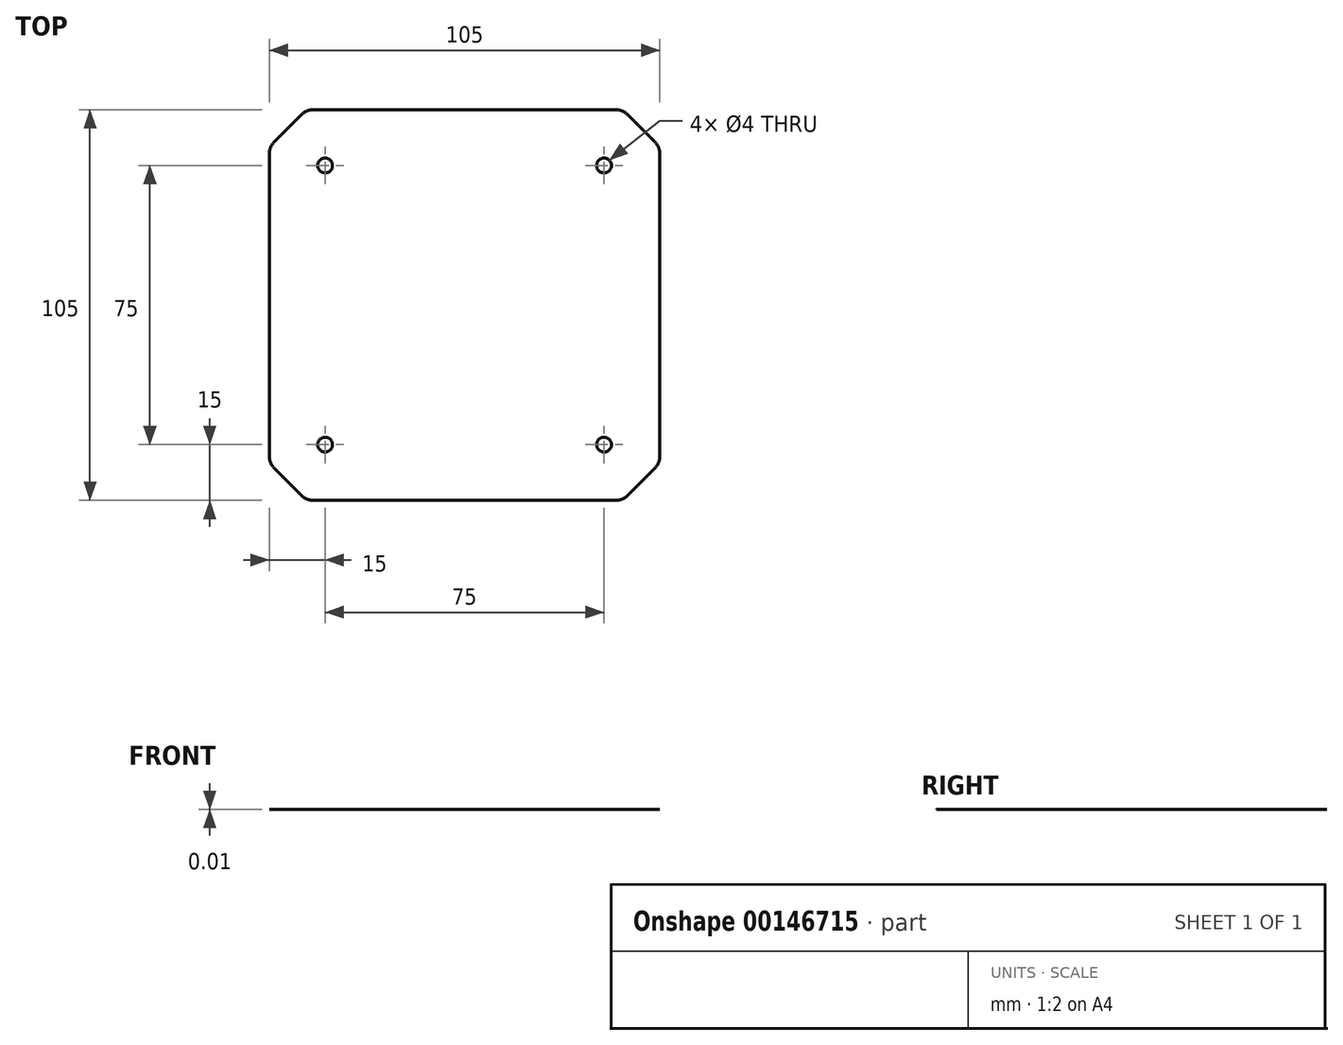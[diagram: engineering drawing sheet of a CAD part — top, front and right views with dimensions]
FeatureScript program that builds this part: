
annotation { "Feature Type Name" : "Feature", "Feature Type Description" : "" }
export const myFeature = defineFeature(function(context is Context, id is Id, definition is map)
    precondition{}
    {
        {
            var Q0;
            Q0=qCreatedBy(makeId("Top.planeOp"),FACE);
            var sketch = newSketch(context, id + "F0", { "sketchPlane" : qUnion([Q0])});
            skCircle(sketch, "E0", {"center": v(-37.5, 37.5) * mm, "radius": 2 * mm});
            skCircle(sketch, "E1.MirrorC", {"center": v(37.5, 37.5) * mm, "radius": 2 * mm});
            skCircle(sketch, "E2.MirrorC", {"center": v(-37.5, -37.5) * mm, "radius": 2 * mm});
            skCircle(sketch, "E3.MirrorC", {"center": v(37.5, -37.5) * mm, "radius": 2 * mm});
            skLineSegment(sketch, "E4.bottom", {"start": v(-52.5, 52.5) * mm, "end": v(52.5, 52.5) * mm});
            skLineSegment(sketch, "E4.top", {"start": v(-52.5, -52.5) * mm, "end": v(52.5, -52.5) * mm});
            skLineSegment(sketch, "E4.left", {"start": v(-52.5, 52.5) * mm, "end": v(-52.5, -52.5) * mm});
            skLineSegment(sketch, "E4.right", {"start": v(52.5, 52.5) * mm, "end": v(52.5, -52.5) * mm});
            skSolve(sketch);
        }
        {
            var Q0;
            Q0=makeQuery(id+"F0.imprint","IMPRINT",FACE,{"disambiguationData":[TD([[makeQuery(id+"F0.imprint","IMPRINT",EDGE,{"derivedFrom":sQuery(id+"F0.wireOp",EDGE,"E0")}),-1.0]])]});
            extrude(context, id + "F1", {"entities" : qUnion([Q0]), "depth" : 1 / 101.6 * mm});
        }
        {
            var Q0;
            Q0=makeQuery(id+"F1.opExtrude","SWEPT_EDGE",EDGE,{"disambiguationData":[OSD([sQuery(id+"F0.wireOp",EDGE,"E4.top"),sQuery(id+"F0.wireOp",EDGE,"E4.left")])]});
            var Q1;
            Q1=makeQuery(id+"F1.opExtrude","SWEPT_EDGE",EDGE,{"disambiguationData":[OSD([sQuery(id+"F0.wireOp",EDGE,"E4.top"),sQuery(id+"F0.wireOp",EDGE,"E4.right")])]});
            var Q2;
            Q2=makeQuery(id+"F1.opExtrude","SWEPT_EDGE",EDGE,{"disambiguationData":[OSD([sQuery(id+"F0.wireOp",EDGE,"E4.bottom"),sQuery(id+"F0.wireOp",EDGE,"E4.right")])]});
            var Q3;
            Q3=makeQuery(id+"F1.opExtrude","SWEPT_EDGE",EDGE,{"disambiguationData":[OSD([sQuery(id+"F0.wireOp",EDGE,"E4.bottom"),sQuery(id+"F0.wireOp",EDGE,"E4.left")])]});
            chamfer(context, id + "F2", {"entities" : qUnion([Q0, Q1, Q2, Q3]), "width" : 10 * mm, "tangentPropagation" : true});
        }
        {
            var Q0;
            {var subQ0=sQuery(id+"F0.wireOp",EDGE,"E4.right");Q0=makeQuery(id+"F2.opChamfer","BLEND_EDGE",EDGE,{"blendedFrom":[makeQuery(id+"F1.opExtrude","SWEPT_EDGE",EDGE,{"disambiguationData":[OSD([sQuery(id+"F0.wireOp",EDGE,"E4.bottom"),subQ0])]}),makeQuery(id+"F1.opExtrude","SWEPT_FACE",FACE,{"disambiguationData":[OSD([subQ0])]})],"blendedInto":[makeQuery(id+"F1.opExtrude","SWEPT_FACE",FACE,{"disambiguationData":[OSD([subQ0])]})]});}
            var Q1;
            {var subQ0=sQuery(id+"F0.wireOp",EDGE,"E4.bottom");Q1=makeQuery(id+"F2.opChamfer","BLEND_EDGE",EDGE,{"blendedFrom":[makeQuery(id+"F1.opExtrude","SWEPT_EDGE",EDGE,{"disambiguationData":[OSD([subQ0,sQuery(id+"F0.wireOp",EDGE,"E4.right")])]}),makeQuery(id+"F1.opExtrude","SWEPT_FACE",FACE,{"disambiguationData":[OSD([subQ0])]})],"blendedInto":[makeQuery(id+"F1.opExtrude","SWEPT_FACE",FACE,{"disambiguationData":[OSD([subQ0])]})]});}
            var Q2;
            {var subQ0=sQuery(id+"F0.wireOp",EDGE,"E4.bottom");Q2=makeQuery(id+"F2.opChamfer","BLEND_EDGE",EDGE,{"blendedFrom":[makeQuery(id+"F1.opExtrude","SWEPT_EDGE",EDGE,{"disambiguationData":[OSD([subQ0,sQuery(id+"F0.wireOp",EDGE,"E4.left")])]}),makeQuery(id+"F1.opExtrude","SWEPT_FACE",FACE,{"disambiguationData":[OSD([subQ0])]})],"blendedInto":[makeQuery(id+"F1.opExtrude","SWEPT_FACE",FACE,{"disambiguationData":[OSD([subQ0])]})]});}
            var Q3;
            {var subQ0=sQuery(id+"F0.wireOp",EDGE,"E4.left");Q3=makeQuery(id+"F2.opChamfer","BLEND_EDGE",EDGE,{"blendedFrom":[makeQuery(id+"F1.opExtrude","SWEPT_EDGE",EDGE,{"disambiguationData":[OSD([sQuery(id+"F0.wireOp",EDGE,"E4.bottom"),subQ0])]}),makeQuery(id+"F1.opExtrude","SWEPT_FACE",FACE,{"disambiguationData":[OSD([subQ0])]})],"blendedInto":[makeQuery(id+"F1.opExtrude","SWEPT_FACE",FACE,{"disambiguationData":[OSD([subQ0])]})]});}
            var Q4;
            {var subQ0=sQuery(id+"F0.wireOp",EDGE,"E4.left");Q4=makeQuery(id+"F2.opChamfer","BLEND_EDGE",EDGE,{"blendedFrom":[makeQuery(id+"F1.opExtrude","SWEPT_EDGE",EDGE,{"disambiguationData":[OSD([sQuery(id+"F0.wireOp",EDGE,"E4.top"),subQ0])]}),makeQuery(id+"F1.opExtrude","SWEPT_FACE",FACE,{"disambiguationData":[OSD([subQ0])]})],"blendedInto":[makeQuery(id+"F1.opExtrude","SWEPT_FACE",FACE,{"disambiguationData":[OSD([subQ0])]})]});}
            var Q5;
            {var subQ0=sQuery(id+"F0.wireOp",EDGE,"E4.top");Q5=makeQuery(id+"F2.opChamfer","BLEND_EDGE",EDGE,{"blendedFrom":[makeQuery(id+"F1.opExtrude","SWEPT_EDGE",EDGE,{"disambiguationData":[OSD([subQ0,sQuery(id+"F0.wireOp",EDGE,"E4.left")])]}),makeQuery(id+"F1.opExtrude","SWEPT_FACE",FACE,{"disambiguationData":[OSD([subQ0])]})],"blendedInto":[makeQuery(id+"F1.opExtrude","SWEPT_FACE",FACE,{"disambiguationData":[OSD([subQ0])]})]});}
            var Q6;
            {var subQ0=sQuery(id+"F0.wireOp",EDGE,"E4.top");Q6=makeQuery(id+"F2.opChamfer","BLEND_EDGE",EDGE,{"blendedFrom":[makeQuery(id+"F1.opExtrude","SWEPT_EDGE",EDGE,{"disambiguationData":[OSD([subQ0,sQuery(id+"F0.wireOp",EDGE,"E4.right")])]}),makeQuery(id+"F1.opExtrude","SWEPT_FACE",FACE,{"disambiguationData":[OSD([subQ0])]})],"blendedInto":[makeQuery(id+"F1.opExtrude","SWEPT_FACE",FACE,{"disambiguationData":[OSD([subQ0])]})]});}
            var Q7;
            {var subQ0=sQuery(id+"F0.wireOp",EDGE,"E4.right");Q7=makeQuery(id+"F2.opChamfer","BLEND_EDGE",EDGE,{"blendedFrom":[makeQuery(id+"F1.opExtrude","SWEPT_EDGE",EDGE,{"disambiguationData":[OSD([sQuery(id+"F0.wireOp",EDGE,"E4.top"),subQ0])]}),makeQuery(id+"F1.opExtrude","SWEPT_FACE",FACE,{"disambiguationData":[OSD([subQ0])]})],"blendedInto":[makeQuery(id+"F1.opExtrude","SWEPT_FACE",FACE,{"disambiguationData":[OSD([subQ0])]})]});}
            fillet(context, id + "F3", {"entities" : qUnion([Q0, Q1, Q2, Q3, Q4, Q5, Q6, Q7]), "radius" : 5 * mm, "tangentPropagation" : true, "allowEdgeOverflow" : false});
        }
    });
